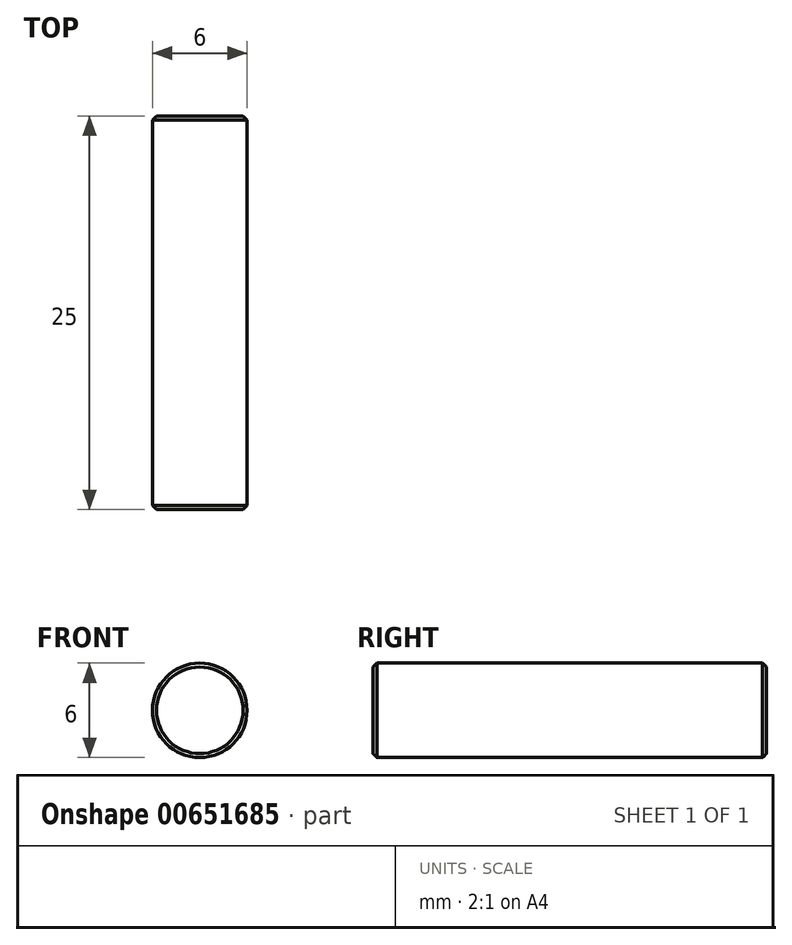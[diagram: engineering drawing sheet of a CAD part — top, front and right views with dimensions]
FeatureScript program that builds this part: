
annotation { "Feature Type Name" : "Feature", "Feature Type Description" : "" }
export const myFeature = defineFeature(function(context is Context, id is Id, definition is map)
    precondition{}
    {
        {
            var Q0;
            Q0=qCreatedBy(makeId("Front.planeOp"),FACE);
            var sketch = newSketch(context, id + "F0", { "sketchPlane" : qUnion([Q0])});
            skCircle(sketch, "E0", {"center": v(0, 0) * mm, "radius": 3 * mm});
            skSolve(sketch);
        }
        {
            var Q0;
            Q0=makeQuery(id+"F0.imprint","IMPRINT",FACE,{"disambiguationData":[TD([[makeQuery(id+"F0.imprint","IMPRINT",EDGE,{"derivedFrom":sQuery(id+"F0.wireOp",EDGE,"E0")}),1.0]])]});
            extrude(context, id + "F1", {"entities" : qUnion([Q0]), "depth" : 25 * mm, "offsetDistance" : 25 * mm});
        }
        {
            var Q0;
            Q0=makeQuery(id+"F1.opExtrude","CAP_EDGE",EDGE,{"disambiguationData":[OSD([sQuery(id+"F0.wireOp",EDGE,"E0")])],"isStart":true});
            var Q1;
            Q1=makeQuery(id+"F1.opExtrude","CAP_EDGE",EDGE,{"disambiguationData":[OSD([sQuery(id+"F0.wireOp",EDGE,"E0")])],"isStart":false});
            chamfer(context, id + "F2", {"entities" : qUnion([Q0, Q1]), "width" : .25 * mm, "tangentPropagation" : true});
        }
    });
